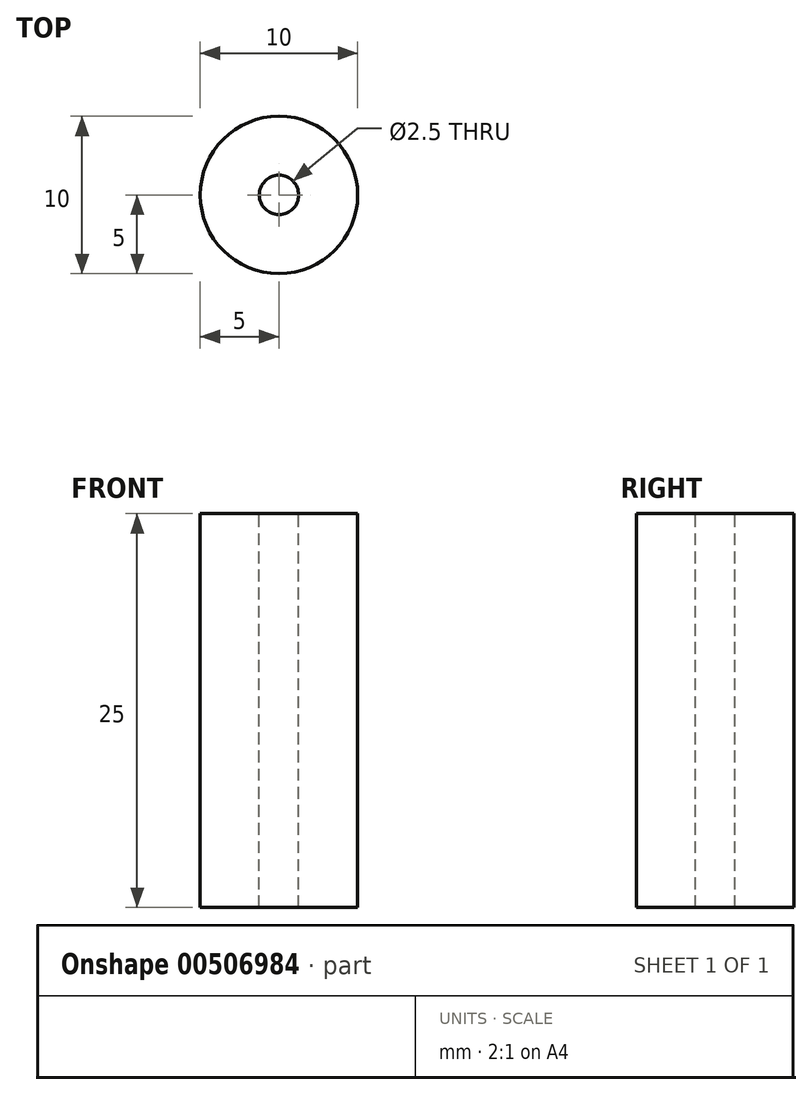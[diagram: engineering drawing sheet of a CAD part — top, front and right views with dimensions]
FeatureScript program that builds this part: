
annotation { "Feature Type Name" : "Feature", "Feature Type Description" : "" }
export const myFeature = defineFeature(function(context is Context, id is Id, definition is map)
    precondition{}
    {
        {
            var Q0;
            Q0=qCreatedBy(makeId("Top.planeOp"),FACE);
            var sketch = newSketch(context, id + "F0", { "sketchPlane" : qUnion([Q0])});
            skCircle(sketch, "E0", {"center": v(0, 0) * mm, "radius": 5 * mm});
            skSolve(sketch);
        }
        {
            var Q0;
            Q0=makeQuery(id+"F0.imprint","IMPRINT",FACE,{"disambiguationData":[TD([[makeQuery(id+"F0.imprint","IMPRINT",EDGE,{"derivedFrom":sQuery(id+"F0.wireOp",EDGE,"E0")}),1.0]])]});
            extrude(context, id + "F1", {"entities" : qUnion([Q0]), "depth" : 25 * mm, "offsetDistance" : 25 * mm});
        }
        {
            var Q0;
            Q0=makeQuery(id+"F1.opExtrude","CAP_FACE",FACE,{"disambiguationData":[OSD([sQuery(id+"F0.wireOp",EDGE,"E0")])],"isStart":false});
            var sketch = newSketch(context, id + "F2", { "sketchPlane" : qUnion([Q0])});
            skPoint(sketch, "E1.0", {"position": v(0, 0) * mm});
            skSolve(sketch);
        }
        {
            var Q0;
            Q0=sQuery(id+"F2.wireOp",VERTEX,"E1.0");
            var Q1;
            Q1=makeQuery(id+"F1.opExtrude","SWEPT_BODY",BODY,{"disambiguationData":[OSD([sQuery(id+"F0.wireOp",EDGE,"E0")])]});
            hole(context, id + "F3", {"style" : HoleStyle.SIMPLE, "endStyle" : HoleEndStyle.THROUGH, "standardTappedOrClearance" : lookupTablePath({ "standard" : "ISO", "engagement" : "75%", "pitch" : "0.5 mm", "size" : "M3", "type" : "Tapped" }), "standardBlindInLast" : lookupTablePath({ "standard" : "ISO", "engagement" : "75%", "pitch" : "0.5 mm", "size" : "M3", "type" : "Tapped" }), "holeDiameter" : 2.5 * mm, "showTappedDepth" : true, "isTappedThrough" : true, "tappedDepth" : 12 * mm, "tapClearance" : 3, "startFromSketch" : true, "locations" : qUnion([Q0]), "scope" : qUnion([Q1]), "majorDiameter" : 3 * mm});
        }
    });
